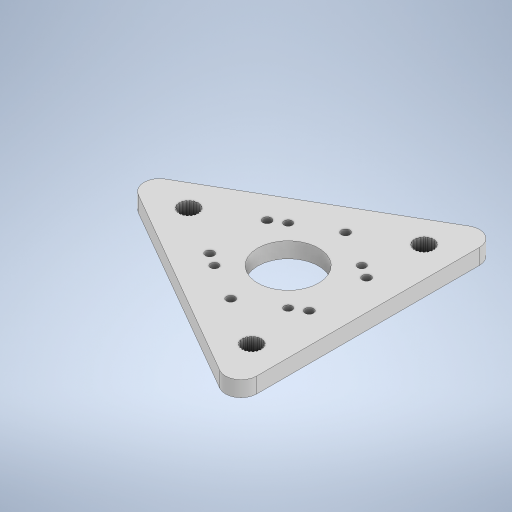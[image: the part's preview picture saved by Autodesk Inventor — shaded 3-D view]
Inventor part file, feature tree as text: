
AUTODESK INVENTOR PART (.ipt)
format: ipt  version: 2024 (Build 280153000, 153)  size: 507,392 bytes
history: native  units: in
note: dims shown in document units (in); Inventor stores cm internally (conversion verified against a paired STEP export)
features: extrude x2, fillet x1, sketch x1
ambient origin geometry x8: Origin, YZ Plane, XZ Plane, XY Plane, X Axis, Y Axis, Z Axis, Center Point
bodies: Solid1 (feature_tree)
feature tree (4):
  extrude  "Extrusion1"  Depth=0.3937in
  fillet  "Fillet1"  Radius=4.0415in
  extrude  "Extrusion2"  Depth=0.3937in
  sketch  "Sketch3"  dims[d0=7.0in d1=1.5394in d2=4.0415in d3=2.5161in d4=0.481in d5=120.0deg d6=120.0deg d7=0.3937in d8=0.0in d9=0.3937in d11=0.0203in d12=0.2407in d13=7.874in d15=360.0deg d17=1.1811in d19=360.0deg d21=0.2047in d22=0.2047in d23=1.8638in d24=1.8638in d25=0.9319in d26=0.9319in d27=0.2165in d28=4.358in d29=1.4527in d30=1.4527in d31=1.4527in d32=1.4527in d33=1.4527in d34=1.4527in d35=0.3937in d36=0.0in]
